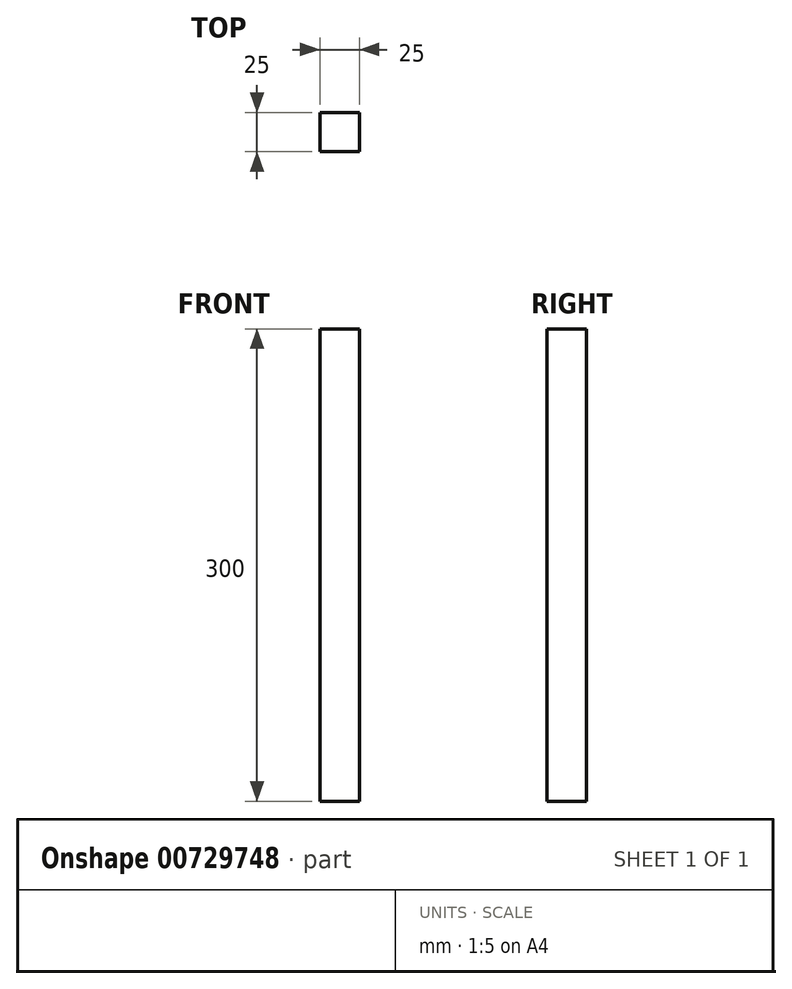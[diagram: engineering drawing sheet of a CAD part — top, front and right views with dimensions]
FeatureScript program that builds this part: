
annotation { "Feature Type Name" : "Feature", "Feature Type Description" : "" }
export const myFeature = defineFeature(function(context is Context, id is Id, definition is map)
    precondition{}
    {
        {
            var Q0;
            Q0=qCreatedBy(makeId("Top.planeOp"),FACE);
            var sketch = newSketch(context, id + "F0", { "sketchPlane" : qUnion([Q0])});
            skLineSegment(sketch, "E0.bottom", {"start": v(-12.64, 9.97) * mm, "end": v(12.36, 9.97) * mm});
            skLineSegment(sketch, "E0.top", {"start": v(-12.64, -15.03) * mm, "end": v(12.36, -15.03) * mm});
            skLineSegment(sketch, "E0.left", {"start": v(-12.64, 9.97) * mm, "end": v(-12.64, -15.03) * mm});
            skLineSegment(sketch, "E0.right", {"start": v(12.36, 9.97) * mm, "end": v(12.36, -15.03) * mm});
            skSolve(sketch);
        }
        {
            var Q0;
            Q0=makeQuery(id+"F0.imprint","IMPRINT",FACE,{"disambiguationData":[TD([[makeQuery(id+"F0.imprint","IMPRINT",EDGE,{"derivedFrom":sQuery(id+"F0.wireOp",EDGE,"E0.bottom")}),-1.0]])]});
            extrude(context, id + "F1", {"entities" : qUnion([Q0]), "oppositeDirection" : true, "depth" : 300 * mm, "offsetDistance" : 25 * mm});
        }
    });
